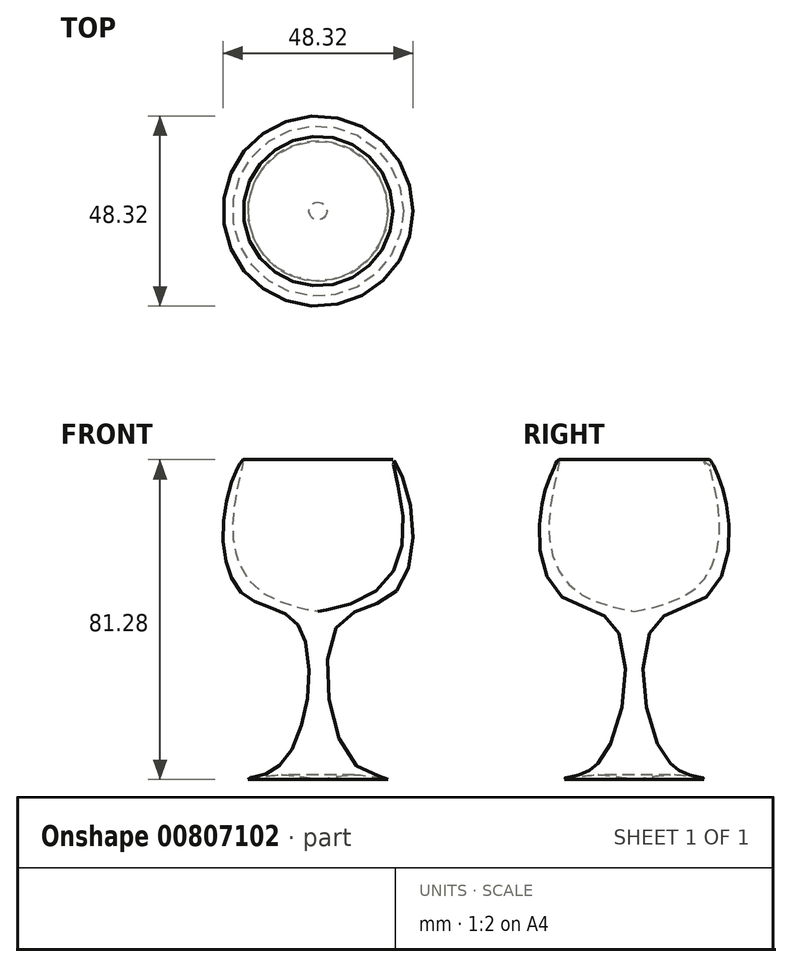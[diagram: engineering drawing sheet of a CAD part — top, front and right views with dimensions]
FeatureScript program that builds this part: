
annotation { "Feature Type Name" : "Feature", "Feature Type Description" : "" }
export const myFeature = defineFeature(function(context is Context, id is Id, definition is map)
    precondition{}
    {
        {
            var Q0;
            Q0=qCreatedBy(makeId("Front.planeOp"),FACE);
            var sketch = newSketch(context, id + "F0", { "sketchPlane" : qUnion([Q0])});
            skFitSpline(sketch, "E0", {"points": [v(0, 0) * mm, v(0, 42.68) * mm, v(0.13, 42.8) * mm, v(14.07, 47.44) * mm, v(21.58, 66.92) * mm, v(19.06, 81.27) * mm, v(23.4, 70.19) * mm, v(18.95, 46.95) * mm, v(4.64, 38.56) * mm, v(10.08, 3.26) * mm, v(17.72, 0) * mm, v(0, 0) * mm]});
            skLineSegment(sketch, "E1", {"start": v(0, 64.48) * mm, "end": v(0, -8.44) * mm});
            skFitSpline(sketch, "E2", {"points": [v(0, 0) * mm, v(7, 1.06) * mm, v(11.44, 1.06) * mm, v(17.72, 0) * mm], "startDerivative": vector(20.47, 3.55) * mm, "endDerivative": vector(19.18, -3.75) * mm});
            skSolve(sketch);
        }
        {
            var Q0;
            {var subQ0=sQuery(id+"F0.wireOp",EDGE,"E2");Q0=makeQuery(id+"F0.imprint","IMPRINT",FACE,{"disambiguationData":[TD([[makeQuery(id+"F0.imprint","IMPRINT",EDGE,{"derivedFrom":subQ0}),1.0]])]});}
            var Q1;
            Q1=sQuery(id+"F0.wireOp",EDGE,"E1");
            revolve(context, id + "F1", {"surfaceOperationType" : NewSurfaceOperationType.NEW, "entities" : qUnion([Q0]), "axis" : qUnion([Q1]), "revolveType" : RevolveType.FULL});
        }
    });
